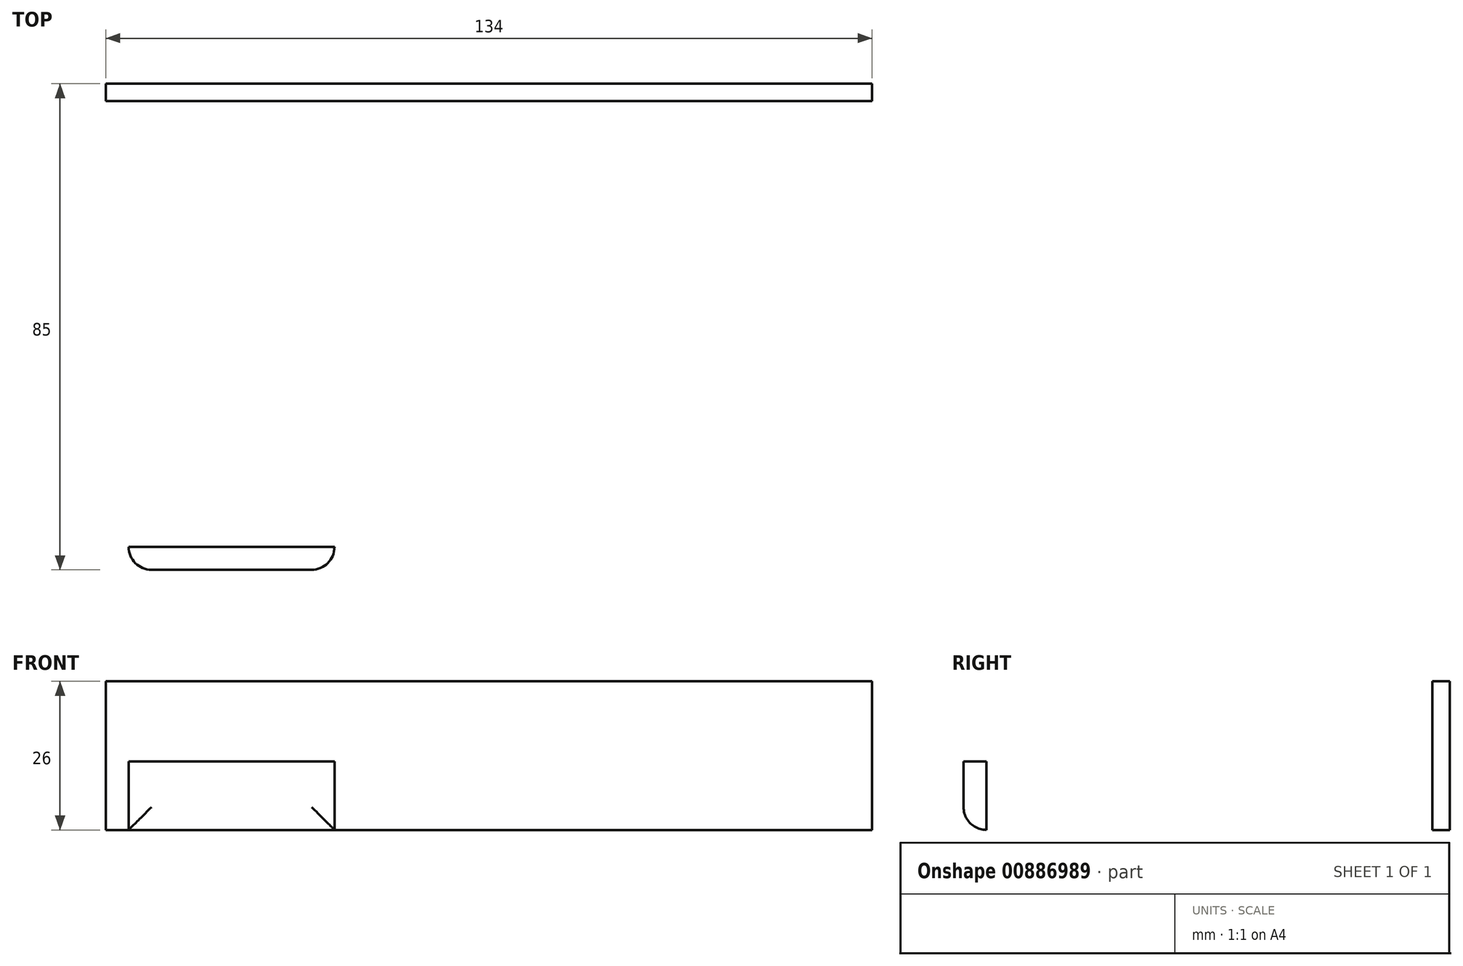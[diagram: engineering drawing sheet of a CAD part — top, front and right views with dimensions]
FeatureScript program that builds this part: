
annotation { "Feature Type Name" : "Feature", "Feature Type Description" : "" }
export const myFeature = defineFeature(function(context is Context, id is Id, definition is map)
    precondition{}
    {
        {
            var Q0;
            Q0=qCreatedBy(makeId("Top.planeOp"),FACE);
            var sketch = newSketch(context, id + "F0", { "sketchPlane" : qUnion([Q0])});
            skLineSegment(sketch, "E0.bottom", {"start": v(0, 0) * mm, "end": v(134, 0) * mm});
            skLineSegment(sketch, "E0.top", {"start": v(0, -85) * mm, "end": v(134, -85) * mm});
            skLineSegment(sketch, "E0.left", {"start": v(0, 0) * mm, "end": v(0, -85) * mm});
            skLineSegment(sketch, "E0.right", {"start": v(134, 0) * mm, "end": v(134, -85) * mm});
            skLineSegment(sketch, "E1", {"start": v(0, -3) * mm, "end": v(134, -3) * mm});
            skLineSegment(sketch, "E2.bottom", {"start": v(4, -85) * mm, "end": v(40, -85) * mm});
            skLineSegment(sketch, "E2.top", {"start": v(4, -81) * mm, "end": v(40, -81) * mm});
            skLineSegment(sketch, "E2.left", {"start": v(4, -85) * mm, "end": v(4, -81) * mm});
            skLineSegment(sketch, "E2.right", {"start": v(40, -85) * mm, "end": v(40, -81) * mm});
            skCircle(sketch, "E3", {"center": v(120, -60) * mm, "radius": 3.75 * mm});
            skCircle(sketch, "E4", {"center": v(120, -25) * mm, "radius": 3.75 * mm});
            skSolve(sketch);
        }
        {
            var Q0;
            {var subQ0=sQuery(id+"F0.wireOp",EDGE,"E1");var subQ12=makeQuery(id+"F0.imprint","IMPRINT",EDGE,{"derivedFrom":subQ0});var subQ13=makeQuery(id+"F0.imprint","IMPRINT",EDGE,{"derivedFrom":sQuery(id+"F0.wireOp",EDGE,"E2.top")});var subQ16=sQuery(id+"F0.wireOp",EDGE,"E0.bottom");Q0=qUnion([makeQuery(id+"F0.imprint","IMPRINT",FACE,{"disambiguationData":[TD([[makeQuery(id+"F0.imprint","IMPRINT",EDGE,{"derivedFrom":subQ16}),-1.0]])]}),makeQuery(id+"F0.imprint","IMPRINT",FACE,{"disambiguationData":[TD([[subQ13,-1.0]])]}),makeQuery(id+"F0.imprint","IMPRINT",FACE,{"disambiguationData":[TD([[subQ12,-1.0]])]})]);}
            extrude(context, id + "F1", {"entities" : qUnion([Q0]), "depth" : 4 * mm, "offsetDistance" : 25 * mm});
        }
        {
            var Q0;
            {var subQ0=sQuery(id+"F0.wireOp",EDGE,"E0.bottom");Q0=makeQuery(id+"F0.imprint","IMPRINT",FACE,{"disambiguationData":[TD([[makeQuery(id+"F0.imprint","IMPRINT",EDGE,{"derivedFrom":subQ0}),-1.0]])]});}
            extrude(context, id + "F2", {"entities" : qUnion([Q0]), "operationType" : NewBodyOperationType.ADD, "depth" : 26 * mm, "offsetDistance" : 25 * mm});
        }
        {
            var Q0;
            Q0=makeQuery(id+"F0.imprint","IMPRINT",FACE,{"disambiguationData":[TD([[makeQuery(id+"F0.imprint","IMPRINT",EDGE,{"derivedFrom":sQuery(id+"F0.wireOp",EDGE,"E2.top")}),-1.0]])]});
            extrude(context, id + "F3", {"entities" : qUnion([Q0]), "operationType" : NewBodyOperationType.ADD, "depth" : 12 * mm, "offsetDistance" : 25 * mm});
        }
        {
            var Q0;
            Q0=makeQuery(id+"F1.opExtrude","CAP_EDGE",EDGE,{"disambiguationData":[OSD([sQuery(id+"F0.wireOp",EDGE,"E0.top")])],"isStart":true});
            var Q1;
            Q1=makeQuery(id+"F1.opExtrude","CAP_EDGE",EDGE,{"disambiguationData":[OSD([sQuery(id+"F0.wireOp",EDGE,"E0.right")])],"isStart":true});
            var Q2;
            Q2=makeQuery(id+"F1.opExtrude","CAP_EDGE",EDGE,{"disambiguationData":[OSD([sQuery(id+"F0.wireOp",EDGE,"E0.left")])],"isStart":true});
            var Q3;
            Q3=makeQuery(id+"F1.opExtrude","CAP_EDGE",EDGE,{"disambiguationData":[OSD([sQuery(id+"F0.wireOp",EDGE,"E0.bottom")])],"isStart":true});
            var Q4;
            {var subQ0=sQuery(id+"F0.wireOp",EDGE,"E0.right");var subQ1=sQuery(id+"F0.wireOp",EDGE,"E0.bottom");Q4=makeQuery(id+"F2.boolean.opBoolean","MERGE",EDGE,{"derivedFrom":[makeQuery(id+"F1.opExtrude","SWEPT_EDGE",EDGE,{"disambiguationData":[OSD([subQ1,subQ0])]}),makeQuery(id+"F2.opExtrude","SWEPT_EDGE",EDGE,{"disambiguationData":[OSD([subQ1,subQ0])]})]});}
            var Q5;
            {var subQ0=sQuery(id+"F0.wireOp",EDGE,"E0.left");var subQ1=sQuery(id+"F0.wireOp",EDGE,"E0.bottom");Q5=makeQuery(id+"F2.boolean.opBoolean","MERGE",EDGE,{"derivedFrom":[makeQuery(id+"F1.opExtrude","SWEPT_EDGE",EDGE,{"disambiguationData":[OSD([subQ1,subQ0])]}),makeQuery(id+"F2.opExtrude","SWEPT_EDGE",EDGE,{"disambiguationData":[OSD([subQ1,subQ0])]})]});}
            var Q6;
            Q6=makeQuery(id+"F1.opExtrude","SWEPT_EDGE",EDGE,{"disambiguationData":[OSD([sQuery(id+"F0.wireOp",EDGE,"E0.top"),sQuery(id+"F0.wireOp",EDGE,"E0.right")])]});
            var Q7;
            Q7=makeQuery(id+"F1.opExtrude","SWEPT_EDGE",EDGE,{"disambiguationData":[OSD([sQuery(id+"F0.wireOp",EDGE,"E0.top"),sQuery(id+"F0.wireOp",EDGE,"E0.left")])]});
            fillet(context, id + "F4", {"entities" : qUnion([Q0, Q1, Q2, Q3, Q4, Q5, Q6, Q7]), "radius" : 4 * mm, "allowEdgeOverflow" : false});
        }
    });
